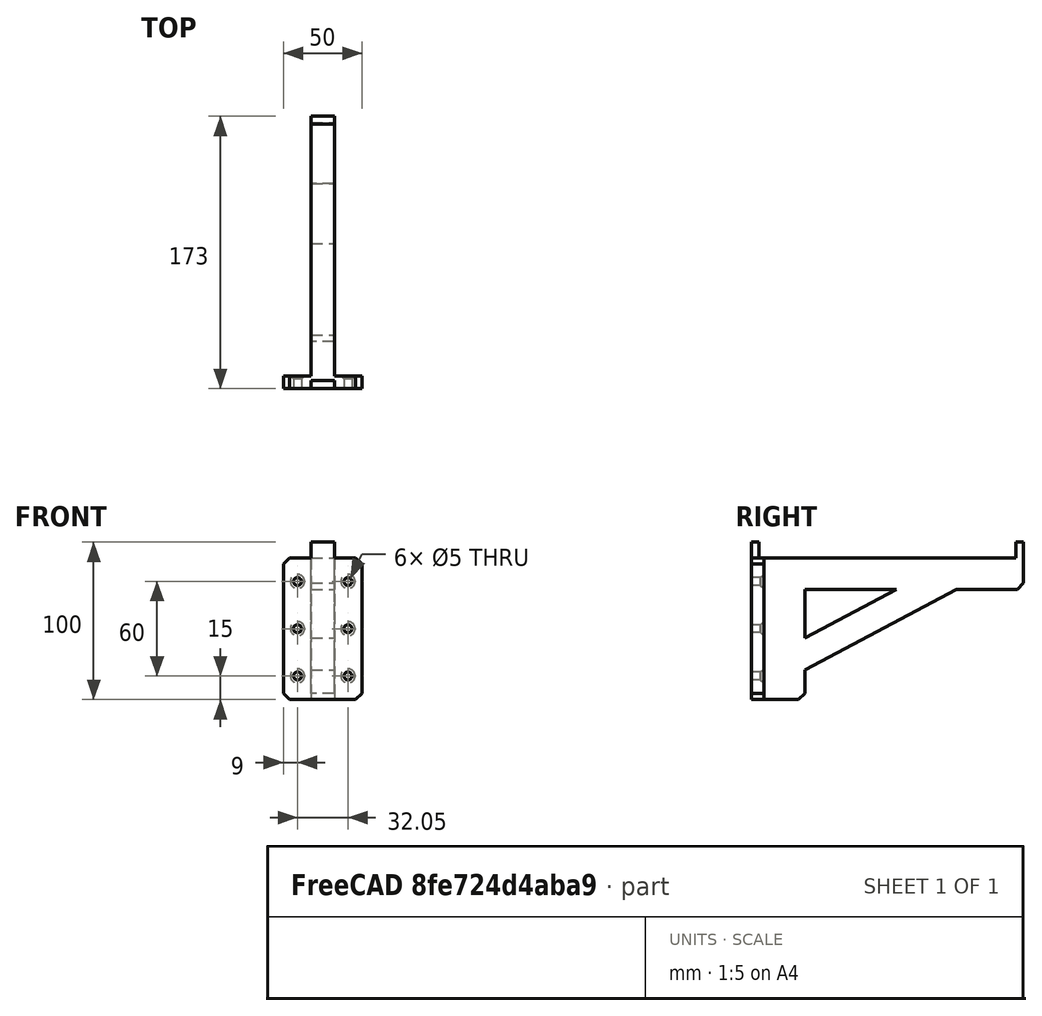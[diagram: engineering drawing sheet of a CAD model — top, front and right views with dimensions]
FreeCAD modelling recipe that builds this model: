
FCSTD DOCUMENT  (FreeCAD 0.15R4671 (Git))
Label: bracket-163mm
License: All rights reserved
LicenseURL: http://en.wikipedia.org/wiki/All_rights_reserved
objects: Part::Cut×8, Part::Cylinder×6, Part::Box×5, Part::Chamfer×4, Part::Fuse×2
note: 25 computed .brp shape members not serialized (recipe doc carries the construction recipe); baked Part::Feature solids carry a one-line shape summary decoded from their .brp

FEATURE [Part::Box] Box  label="Cube"
  Height = 100
  Length = 15
  Width = 173
FEATURE [Part::Box] Box001  label="Cube001"
  Height = 100
  Length = 15
  Placement = pos=(0,34,-30) rot=(0,0,1;0rad)
  Width = 163
FEATURE [Part::Box] Box002  label="Cube002"
  Height = 100
  Length = 15
  Placement = pos=(0,5,90) rot=(0,0,1;0rad)
  Width = 163
FEATURE [Part::Box] Box003  label="Cube003"
  Height = 18
  Length = 15
  Placement = pos=(0,20,11.25) rot=(1,0,0;0.488692rad)
  Width = 125
FEATURE [Part::Cut] Cut
  Base = -> Box
  Tool = -> Box001
FEATURE [Part::Fuse] Fusion
  Base = -> Cut
  Tool = -> Box003
FEATURE [Part::Box] Box004  label="Cube004"
  Height = 90
  Length = 50
  Placement = pos=(-17.5,0,0) rot=(0,0,1;0rad)
  Width = 8
FEATURE [Part::Chamfer] Chamfer
  Base = -> Box004
  Edges = 4 edges r=4: [Edge2,Edge4,Edge6,Edge8]
FEATURE [Part::Chamfer] Chamfer001
  Base = -> Fusion
  Edges = 1 edges r=4: [Edge37]
FEATURE [Part::Fuse] Fusion001
  Base = -> Chamfer
  Tool = -> Chamfer001
FEATURE [Part::Cut] Cut001
  Base = -> Fusion001
  Tool = -> Box002
FEATURE [Part::Cylinder] Cylinder
  Angle = 360
  Height = 20
  Placement = pos=(23.55,14,15) rot=(1,0,0;1.5708rad)
  Radius = 2.5
FEATURE [Part::Cylinder] Cylinder001
  Angle = 360
  Height = 20
  Placement = pos=(-8.5,14,15) rot=(1,0,0;1.5708rad)
  Radius = 2.5
FEATURE [Part::Cylinder] Cylinder002
  Angle = 360
  Height = 20
  Placement = pos=(23.55,14,45) rot=(1,0,0;1.5708rad)
  Radius = 2.5
FEATURE [Part::Cylinder] Cylinder003
  Angle = 360
  Height = 20
  Placement = pos=(-8.5,14,45) rot=(1,0,0;1.5708rad)
  Radius = 2.5
FEATURE [Part::Cylinder] Cylinder004
  Angle = 360
  Height = 20
  Placement = pos=(23.55,14,75) rot=(1,0,0;1.5708rad)
  Radius = 2.5
FEATURE [Part::Cylinder] Cylinder005
  Angle = 360
  Height = 20
  Placement = pos=(-8.5,14,75) rot=(1,0,0;1.5708rad)
  Radius = 2.5
FEATURE [Part::Chamfer] Chamfer002
  Base = -> Cut001
  Edges = 1 edges r=4: [Edge63]
FEATURE [Part::Cut] Cut002
  Base = -> Chamfer002
  Tool = -> Cylinder
FEATURE [Part::Cut] Cut003
  Base = -> Cut002
  Tool = -> Cylinder001
FEATURE [Part::Cut] Cut004
  Base = -> Cut003
  Tool = -> Cylinder002
FEATURE [Part::Cut] Cut005
  Base = -> Cut004
  Tool = -> Cylinder003
FEATURE [Part::Cut] Cut006
  Base = -> Cut005
  Tool = -> Cylinder004
FEATURE [Part::Cut] Cut007
  Base = -> Cut006
  Tool = -> Cylinder005
FEATURE [Part::Chamfer] Chamfer003  label="Final"
  Base = -> Cut007
  Edges = 6 edges r=2: [Edge39,Edge40,Edge41,Edge99,Edge100,Edge101]
